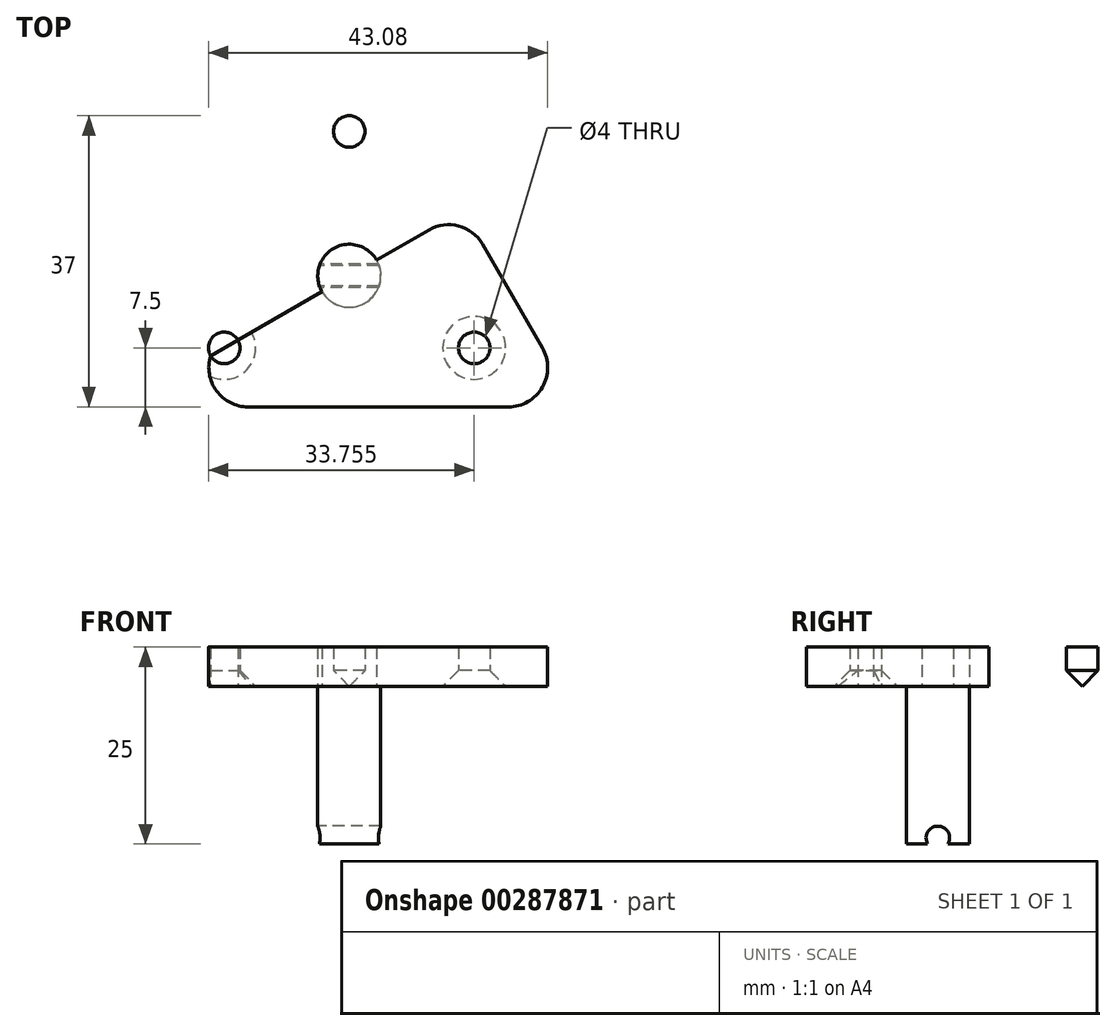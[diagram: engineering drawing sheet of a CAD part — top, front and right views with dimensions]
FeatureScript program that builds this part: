
annotation { "Feature Type Name" : "Feature", "Feature Type Description" : "" }
export const myFeature = defineFeature(function(context is Context, id is Id, definition is map)
    precondition{}
    {
        {
            var Q0;
            Q0=qCreatedBy(makeId("Top.planeOp"),FACE);
            var sketch = newSketch(context, id + "F0", { "sketchPlane" : qUnion([Q0])});
            skLineSegment(sketch, "E0", {"start": v(0, 0) * mm, "end": v(28.87, 50) * mm});
            skLineSegment(sketch, "E1", {"start": v(28.87, 50) * mm, "end": v(57.74, 0) * mm});
            skLineSegment(sketch, "E2", {"start": v(57.74, 0) * mm, "end": v(0, 0) * mm});
            skLineSegment(sketch, "E3", {"start": v(28.87, 50) * mm, "end": v(28.87, 0) * mm});
            skLineSegment(sketch, "E4", {"start": v(0, 0) * mm, "end": v(43.3, 25) * mm});
            skLineSegment(sketch, "E5", {"start": v(57.74, 0) * mm, "end": v(14.43, 25) * mm});
            skLineSegment(sketch, "E6", {"start": v(0, 0) * mm, "end": v(13, 7.5) * mm});
            skLineSegment(sketch, "E7", {"start": v(57.74, 0) * mm, "end": v(44.74, 7.5) * mm});
            skLineSegment(sketch, "E8", {"start": v(28.87, 50) * mm, "end": v(28.87, 35) * mm});
            skCircle(sketch, "E9", {"center": v(28.87, 35) * mm, "radius": 2 * mm});
            skCircle(sketch, "E10", {"center": v(13, 7.5) * mm, "radius": 2 * mm});
            skCircle(sketch, "E11", {"center": v(44.74, 7.5) * mm, "radius": 2 * mm});
            skCircle(sketch, "E12", {"center": v(28.87, 16.67) * mm, "radius": 4 * mm});
            skSolve(sketch);
        }
        {
            var Q0;
            {var subQ3=sQuery(id+"F0.wireOp",EDGE,"E10");var subQ5=sQuery(id+"F0.wireOp",EDGE,"E4");var subQ6=makeQuery(id+"F0.imprint","INTERSECT",VERTEX,{"derivedFrom":[subQ5,subQ3]});Q0=makeQuery(id+"F0.imprint","IMPRINT",FACE,{"disambiguationData":[TD([[makeQuery(id+"F0.imprint","IMPRINT",EDGE,{"disambiguationData":[TD([[subQ6,-1.0]])],"derivedFrom":subQ5}),1.0]])]});}
            var Q1;
            {var subQ3=sQuery(id+"F0.wireOp",EDGE,"E9");var subQ9=sQuery(id+"F0.wireOp",EDGE,"E3");var subQ10=makeQuery(id+"F0.imprint","INTERSECT",VERTEX,{"derivedFrom":[subQ9,subQ3]});Q1=makeQuery(id+"F0.imprint","IMPRINT",FACE,{"disambiguationData":[TD([[makeQuery(id+"F0.imprint","IMPRINT",EDGE,{"disambiguationData":[TD([[subQ10,-1.0]])],"derivedFrom":subQ9}),-1.0]])]});}
            var Q2;
            {var subQ3=sQuery(id+"F0.wireOp",EDGE,"E9");var subQ9=sQuery(id+"F0.wireOp",EDGE,"E3");var subQ10=makeQuery(id+"F0.imprint","INTERSECT",VERTEX,{"derivedFrom":[subQ9,subQ3]});Q2=makeQuery(id+"F0.imprint","IMPRINT",FACE,{"disambiguationData":[TD([[makeQuery(id+"F0.imprint","IMPRINT",EDGE,{"disambiguationData":[TD([[subQ10,-1.0]])],"derivedFrom":subQ9}),1.0]])]});}
            var Q3;
            {var subQ5=sQuery(id+"F0.wireOp",EDGE,"E4");var subQ6=sQuery(id+"F0.wireOp",EDGE,"E1");var subQ7=makeQuery(id+"F0.imprint","INTERSECT",VERTEX,{"derivedFrom":[subQ6,subQ5]});Q3=makeQuery(id+"F0.imprint","IMPRINT",FACE,{"disambiguationData":[TD([[makeQuery(id+"F0.imprint","IMPRINT",EDGE,{"disambiguationData":[TD([[subQ7,1.0]])],"derivedFrom":subQ5}),-1.0]])]});}
            var Q4;
            {var subQ1=sQuery(id+"F0.wireOp",EDGE,"E2");var subQ9=sQuery(id+"F0.wireOp",EDGE,"E3");var subQ10=makeQuery(id+"F0.imprint","INTERSECT",VERTEX,{"derivedFrom":[subQ1,subQ9]});Q4=makeQuery(id+"F0.imprint","IMPRINT",FACE,{"disambiguationData":[TD([[makeQuery(id+"F0.imprint","IMPRINT",EDGE,{"disambiguationData":[TD([[subQ10,1.0]])],"derivedFrom":subQ9}),1.0]])]});}
            var Q5;
            {var subQ1=sQuery(id+"F0.wireOp",EDGE,"E2");var subQ5=sQuery(id+"F0.wireOp",EDGE,"E3");var subQ6=makeQuery(id+"F0.imprint","INTERSECT",VERTEX,{"derivedFrom":[subQ1,subQ5]});Q5=makeQuery(id+"F0.imprint","IMPRINT",FACE,{"disambiguationData":[TD([[makeQuery(id+"F0.imprint","IMPRINT",EDGE,{"disambiguationData":[TD([[subQ6,1.0]])],"derivedFrom":subQ5}),-1.0]])]});}
            var Q6;
            {var subQ0=sQuery(id+"F0.wireOp",EDGE,"E12");var subQ1=sQuery(id+"F0.wireOp",EDGE,"E3");var subQ2=makeQuery(id+"F0.imprint","INTERSECT",VERTEX,{"disambiguationData":[OD(1.0)],"derivedFrom":[subQ1,subQ0]});Q6=makeQuery(id+"F0.imprint","IMPRINT",FACE,{"disambiguationData":[TD([[makeQuery(id+"F0.imprint","IMPRINT",EDGE,{"disambiguationData":[TD([[subQ2,-1.0]])],"derivedFrom":subQ0}),1.0]])]});}
            var Q7;
            {var subQ0=sQuery(id+"F0.wireOp",EDGE,"E12");var subQ1=sQuery(id+"F0.wireOp",EDGE,"E3");var subQ2=makeQuery(id+"F0.imprint","INTERSECT",VERTEX,{"disambiguationData":[OD(1.0)],"derivedFrom":[subQ1,subQ0]});Q7=makeQuery(id+"F0.imprint","IMPRINT",FACE,{"disambiguationData":[TD([[makeQuery(id+"F0.imprint","IMPRINT",EDGE,{"disambiguationData":[TD([[subQ2,1.0]])],"derivedFrom":subQ0}),1.0]])]});}
            var Q8;
            {var subQ0=sQuery(id+"F0.wireOp",EDGE,"E12");var subQ1=sQuery(id+"F0.wireOp",EDGE,"E4");var subQ2=makeQuery(id+"F0.imprint","INTERSECT",VERTEX,{"disambiguationData":[OD(0.0)],"derivedFrom":[subQ1,subQ0]});Q8=makeQuery(id+"F0.imprint","IMPRINT",FACE,{"disambiguationData":[TD([[makeQuery(id+"F0.imprint","IMPRINT",EDGE,{"disambiguationData":[TD([[subQ2,1.0]])],"derivedFrom":subQ0}),1.0]])]});}
            var Q9;
            {var subQ0=sQuery(id+"F0.wireOp",EDGE,"E12");var subQ1=sQuery(id+"F0.wireOp",EDGE,"E3");var subQ2=makeQuery(id+"F0.imprint","INTERSECT",VERTEX,{"disambiguationData":[OD(0.0)],"derivedFrom":[subQ1,subQ0]});Q9=makeQuery(id+"F0.imprint","IMPRINT",FACE,{"disambiguationData":[TD([[makeQuery(id+"F0.imprint","IMPRINT",EDGE,{"disambiguationData":[TD([[subQ2,-1.0]])],"derivedFrom":subQ0}),1.0]])]});}
            var Q10;
            {var subQ0=sQuery(id+"F0.wireOp",EDGE,"E12");var subQ1=sQuery(id+"F0.wireOp",EDGE,"E3");var subQ2=makeQuery(id+"F0.imprint","INTERSECT",VERTEX,{"disambiguationData":[OD(0.0)],"derivedFrom":[subQ1,subQ0]});Q10=makeQuery(id+"F0.imprint","IMPRINT",FACE,{"disambiguationData":[TD([[makeQuery(id+"F0.imprint","IMPRINT",EDGE,{"disambiguationData":[TD([[subQ2,1.0]])],"derivedFrom":subQ0}),1.0]])]});}
            var Q11;
            {var subQ0=sQuery(id+"F0.wireOp",EDGE,"E12");var subQ1=sQuery(id+"F0.wireOp",EDGE,"E4");var subQ2=makeQuery(id+"F0.imprint","INTERSECT",VERTEX,{"disambiguationData":[OD(1.0)],"derivedFrom":[subQ1,subQ0]});Q11=makeQuery(id+"F0.imprint","IMPRINT",FACE,{"disambiguationData":[TD([[makeQuery(id+"F0.imprint","IMPRINT",EDGE,{"disambiguationData":[TD([[subQ2,1.0]])],"derivedFrom":subQ0}),1.0]])]});}
            extrude(context, id + "F1", {"entities" : qUnion([Q0, Q1, Q2, Q3, Q4, Q5, Q6, Q7, Q8, Q9, Q10, Q11]), "depth" : 5 * mm});
        }
        {
            var Q0;
            {var subQ0=sQuery(id+"F0.wireOp",EDGE,"E12");var subQ1=sQuery(id+"F0.wireOp",EDGE,"E4");var subQ2=makeQuery(id+"F0.imprint","INTERSECT",VERTEX,{"disambiguationData":[OD(1.0)],"derivedFrom":[subQ1,subQ0]});Q0=makeQuery(id+"F0.imprint","IMPRINT",FACE,{"disambiguationData":[TD([[makeQuery(id+"F0.imprint","IMPRINT",EDGE,{"disambiguationData":[TD([[subQ2,1.0]])],"derivedFrom":subQ0}),1.0]])]});}
            var Q1;
            {var subQ0=sQuery(id+"F0.wireOp",EDGE,"E12");var subQ1=sQuery(id+"F0.wireOp",EDGE,"E3");var subQ2=makeQuery(id+"F0.imprint","INTERSECT",VERTEX,{"disambiguationData":[OD(0.0)],"derivedFrom":[subQ1,subQ0]});Q1=makeQuery(id+"F0.imprint","IMPRINT",FACE,{"disambiguationData":[TD([[makeQuery(id+"F0.imprint","IMPRINT",EDGE,{"disambiguationData":[TD([[subQ2,1.0]])],"derivedFrom":subQ0}),1.0]])]});}
            var Q2;
            {var subQ0=sQuery(id+"F0.wireOp",EDGE,"E12");var subQ1=sQuery(id+"F0.wireOp",EDGE,"E3");var subQ2=makeQuery(id+"F0.imprint","INTERSECT",VERTEX,{"disambiguationData":[OD(0.0)],"derivedFrom":[subQ1,subQ0]});Q2=makeQuery(id+"F0.imprint","IMPRINT",FACE,{"disambiguationData":[TD([[makeQuery(id+"F0.imprint","IMPRINT",EDGE,{"disambiguationData":[TD([[subQ2,-1.0]])],"derivedFrom":subQ0}),1.0]])]});}
            var Q3;
            {var subQ0=sQuery(id+"F0.wireOp",EDGE,"E12");var subQ1=sQuery(id+"F0.wireOp",EDGE,"E4");var subQ2=makeQuery(id+"F0.imprint","INTERSECT",VERTEX,{"disambiguationData":[OD(0.0)],"derivedFrom":[subQ1,subQ0]});Q3=makeQuery(id+"F0.imprint","IMPRINT",FACE,{"disambiguationData":[TD([[makeQuery(id+"F0.imprint","IMPRINT",EDGE,{"disambiguationData":[TD([[subQ2,1.0]])],"derivedFrom":subQ0}),1.0]])]});}
            var Q4;
            {var subQ0=sQuery(id+"F0.wireOp",EDGE,"E12");var subQ1=sQuery(id+"F0.wireOp",EDGE,"E3");var subQ2=makeQuery(id+"F0.imprint","INTERSECT",VERTEX,{"disambiguationData":[OD(1.0)],"derivedFrom":[subQ1,subQ0]});Q4=makeQuery(id+"F0.imprint","IMPRINT",FACE,{"disambiguationData":[TD([[makeQuery(id+"F0.imprint","IMPRINT",EDGE,{"disambiguationData":[TD([[subQ2,1.0]])],"derivedFrom":subQ0}),1.0]])]});}
            var Q5;
            {var subQ0=sQuery(id+"F0.wireOp",EDGE,"E12");var subQ1=sQuery(id+"F0.wireOp",EDGE,"E3");var subQ2=makeQuery(id+"F0.imprint","INTERSECT",VERTEX,{"disambiguationData":[OD(1.0)],"derivedFrom":[subQ1,subQ0]});Q5=makeQuery(id+"F0.imprint","IMPRINT",FACE,{"disambiguationData":[TD([[makeQuery(id+"F0.imprint","IMPRINT",EDGE,{"disambiguationData":[TD([[subQ2,-1.0]])],"derivedFrom":subQ0}),1.0]])]});}
            extrude(context, id + "F2", {"entities" : qUnion([Q0, Q1, Q2, Q3, Q4, Q5]), "operationType" : NewBodyOperationType.ADD, "oppositeDirection" : true, "depth" : 20 * mm});
        }
        {
            var Q0;
            Q0=qCreatedBy(makeId("Right.planeOp"),FACE);
            var sketch = newSketch(context, id + "F3", { "sketchPlane" : qUnion([Q0])});
            skLineSegment(sketch, "E13", {"start": v(0, 0) * mm, "end": v(0, -19.25) * mm});
            skLineSegment(sketch, "E14", {"start": v(0, -19.25) * mm, "end": v(16.66, -19.25) * mm});
            skCircle(sketch, "E15", {"center": v(16.66, -19.25) * mm, "radius": 1.5 * mm});
            skSolve(sketch);
        }
        {
            var Q0;
            Q0 = qSketchRegion(id + "F3", true);
            extrude(context, id + "F4", {"entities" : qUnion([Q0]), "operationType" : NewBodyOperationType.REMOVE, "depth" : 37.6 * mm});
        }
        {
            var Q0;
            Q0=makeQuery(id+"F1.opExtrude","CAP_EDGE",EDGE,{"disambiguationData":[OSD([sQuery(id+"F0.wireOp",EDGE,"E10")])],"isStart":true});
            var Q1;
            Q1=makeQuery(id+"F1.opExtrude","CAP_EDGE",EDGE,{"disambiguationData":[OSD([sQuery(id+"F0.wireOp",EDGE,"E9")])],"isStart":true});
            var Q2;
            Q2=makeQuery(id+"F1.opExtrude","CAP_EDGE",EDGE,{"disambiguationData":[OSD([sQuery(id+"F0.wireOp",EDGE,"E11")])],"isStart":true});
            chamfer(context, id + "F5", {"entities" : qUnion([Q0, Q1, Q2]), "width" : 2 * mm, "tangentPropagation" : true});
        }
        {
            var Q0;
            Q0=makeQuery(id+"F1.opExtrude","SWEPT_EDGE",EDGE,{"disambiguationData":[OSD([sQuery(id+"F0.wireOp",EDGE,"E1"),sQuery(id+"F0.wireOp",EDGE,"E2"),sQuery(id+"F0.wireOp",EDGE,"E7")])]});
            var Q1;
            Q1=makeQuery(id+"F1.opExtrude","SWEPT_EDGE",EDGE,{"disambiguationData":[OSD([sQuery(id+"F0.wireOp",EDGE,"E0"),sQuery(id+"F0.wireOp",EDGE,"E2"),sQuery(id+"F0.wireOp",EDGE,"E6")])]});
            var Q2;
            Q2=makeQuery(id+"F1.opExtrude","SWEPT_EDGE",EDGE,{"disambiguationData":[OSD([sQuery(id+"F0.wireOp",EDGE,"E0"),sQuery(id+"F0.wireOp",EDGE,"E1"),sQuery(id+"F0.wireOp",EDGE,"E8")])]});
            fillet(context, id + "F6", {"entities" : qUnion([Q0, Q1, Q2]), "radius" : 5 * mm, "tangentPropagation" : true, "allowEdgeOverflow" : false});
        }
    });
